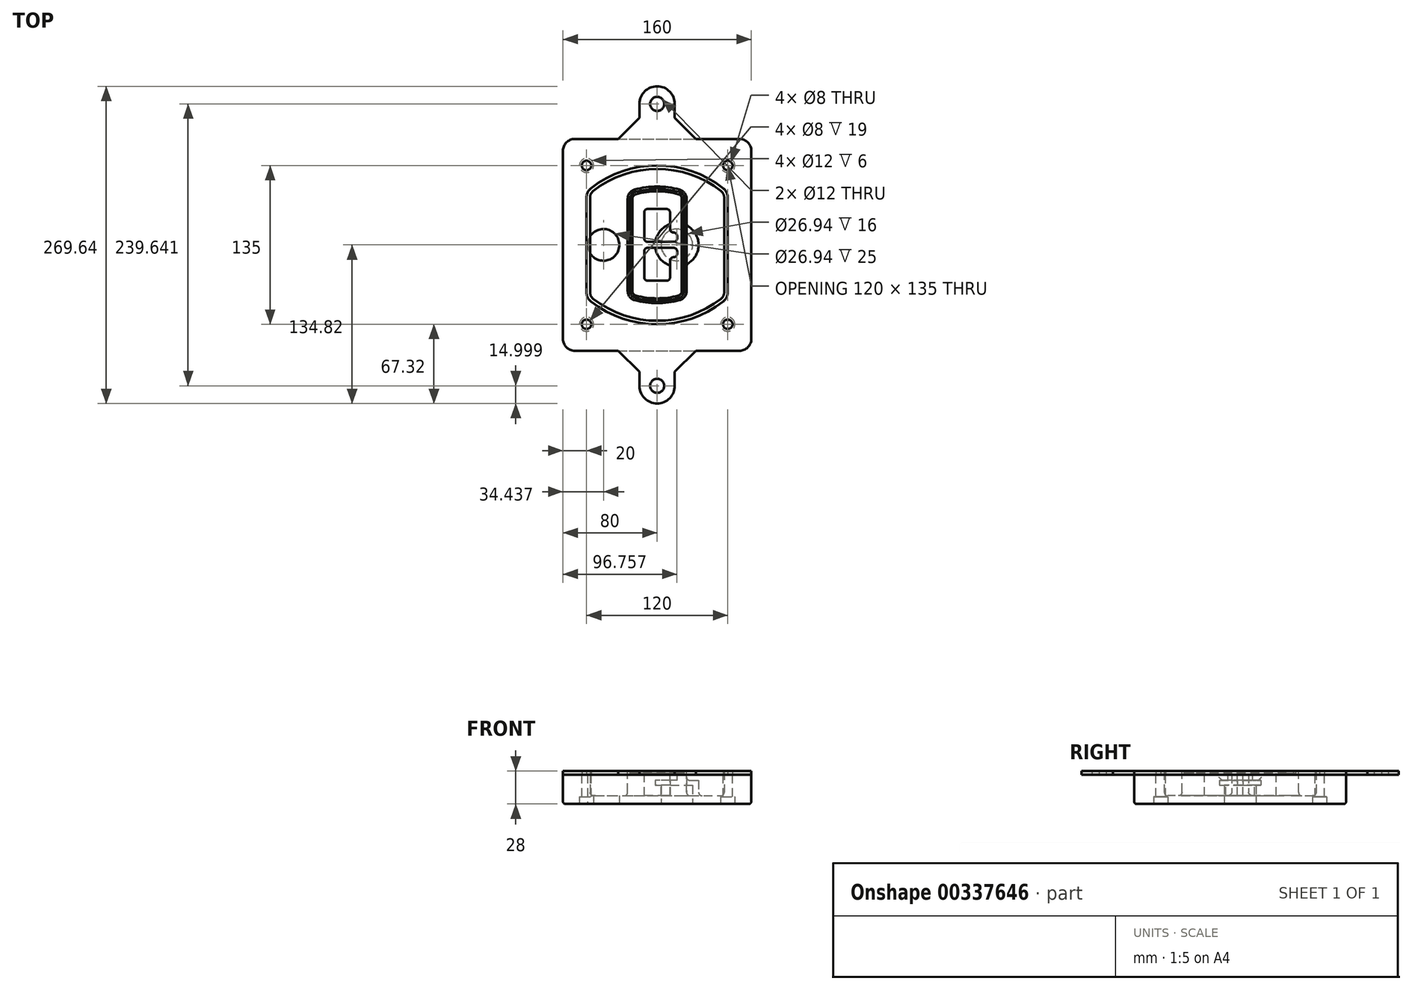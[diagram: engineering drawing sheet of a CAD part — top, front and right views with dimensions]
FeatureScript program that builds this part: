
annotation { "Feature Type Name" : "Feature", "Feature Type Description" : "" }
export const myFeature = defineFeature(function(context is Context, id is Id, definition is map)
    precondition{}
    {
        {
            var Q0;
            Q0=qCreatedBy(makeId("Top.planeOp"),FACE);
            var sketch = newSketch(context, id + "F0", { "sketchPlane" : qUnion([Q0])});
            skPoint(sketch, "E0.rect.middle", {"position": v(0, 0) * mm});
            skLineSegment(sketch, "E1.bottom", {"start": v(-70, -90) * mm, "end": v(70, -90) * mm});
            skLineSegment(sketch, "E1.top", {"start": v(-70, 90) * mm, "end": v(70, 90) * mm});
            skLineSegment(sketch, "E1.left", {"start": v(-80, -80) * mm, "end": v(-80, 80) * mm});
            skLineSegment(sketch, "E1.right", {"start": v(80, -80) * mm, "end": v(80, 80) * mm});
            skLineSegment(sketch, "E2", {"start": v(-80, 90) * mm, "end": v(80, -90) * mm, "construction": true});
            skLineSegment(sketch, "E3", {"start": v(80, 90) * mm, "end": v(-80, -90) * mm, "construction": true});
            skCircle(sketch, "E4", {"center": v(-60, 67.5) * mm, "radius": 4 * mm});
            skCircle(sketch, "E5", {"center": v(60, 67.5) * mm, "radius": 4 * mm});
            skCircle(sketch, "E6", {"center": v(60, -67.5) * mm, "radius": 4 * mm});
            skCircle(sketch, "E7", {"center": v(-60, -67.5) * mm, "radius": 4 * mm});
            skLineSegment(sketch, "E8", {"start": v(-60, 67.5) * mm, "end": v(60, 67.5) * mm, "construction": true});
            skLineSegment(sketch, "E9", {"start": v(60, 67.5) * mm, "end": v(60, -67.5) * mm, "construction": true});
            skLineSegment(sketch, "E10", {"start": v(60, -67.5) * mm, "end": v(-60, -67.5) * mm, "construction": true});
            skLineSegment(sketch, "E11", {"start": v(-60, -67.5) * mm, "end": v(-60, 67.5) * mm, "construction": true});
            skLineSegment(sketch, "E12", {"start": v(-60, 40.3) * mm, "end": v(-60, -40.3) * mm});
            skLineSegment(sketch, "E13", {"start": v(60, 40.3) * mm, "end": v(60, -40.3) * mm});
            skArc(sketch, "E14", {"start": v(56.15, 48.18) * mm, "mid": v(0, 67.5) * mm, "end": v(-56.15, 48.18) * mm});
            skArc(sketch, "E15", {"start": v(-56.15, -48.18) * mm, "mid": v(0, -67.5) * mm, "end": v(56.15, -48.18) * mm});
            skLineSegment(sketch, "E16", {"start": v(-60, 0) * mm, "end": v(60, 0) * mm, "construction": true});
            skPoint(sketch, "E17.visualSharp", {"position": v(-60, -45) * mm});
            skArc(sketch, "E17.filletArc", {"start": v(-60, -40.3) * mm, "mid": v(-58.99, -44.68) * mm, "end": v(-56.15, -48.18) * mm});
            skPoint(sketch, "E18.visualSharp", {"position": v(-60, 45) * mm});
            skArc(sketch, "E18.filletArc", {"start": v(-56.15, 48.18) * mm, "mid": v(-58.99, 44.68) * mm, "end": v(-60, 40.3) * mm});
            skPoint(sketch, "E19.visualSharp", {"position": v(60, 45) * mm});
            skArc(sketch, "E19.filletArc", {"start": v(60, 40.3) * mm, "mid": v(58.99, 44.68) * mm, "end": v(56.15, 48.18) * mm});
            skPoint(sketch, "E20.visualSharp", {"position": v(60, -45) * mm});
            skArc(sketch, "E20.filletArc", {"start": v(56.15, -48.18) * mm, "mid": v(58.99, -44.68) * mm, "end": v(60, -40.3) * mm});
            skPoint(sketch, "E21.visualSharp", {"position": v(-80, 90) * mm});
            skArc(sketch, "E21.filletArc", {"start": v(-70, 90) * mm, "mid": v(-77.07, 87.07) * mm, "end": v(-80, 80) * mm});
            skPoint(sketch, "E22.visualSharp", {"position": v(80, 90) * mm});
            skArc(sketch, "E22.filletArc", {"start": v(80, 80) * mm, "mid": v(77.07, 87.07) * mm, "end": v(70, 90) * mm});
            skPoint(sketch, "E23.visualSharp", {"position": v(80, -90) * mm});
            skArc(sketch, "E23.filletArc", {"start": v(70, -90) * mm, "mid": v(77.07, -87.07) * mm, "end": v(80, -80) * mm});
            skPoint(sketch, "E24.visualSharp", {"position": v(-80, -90) * mm});
            skArc(sketch, "E24.filletArc", {"start": v(-80, -80) * mm, "mid": v(-77.07, -87.07) * mm, "end": v(-70, -90) * mm});
            skArc(sketch, "E25.0", {"start": v(57, 40.3) * mm, "mid": v(56.3, 43.36) * mm, "end": v(54.3, 45.81) * mm});
            skLineSegment(sketch, "E25.1", {"start": v(57, 40.3) * mm, "end": v(57, -40.3) * mm});
            skArc(sketch, "E25.2", {"start": v(54.3, -45.81) * mm, "mid": v(56.3, -43.36) * mm, "end": v(57, -40.3) * mm});
            skArc(sketch, "E25.3", {"start": v(-54.3, -45.81) * mm, "mid": v(0, -64.5) * mm, "end": v(54.3, -45.81) * mm});
            skArc(sketch, "E25.4", {"start": v(-57, -40.3) * mm, "mid": v(-56.3, -43.36) * mm, "end": v(-54.3, -45.81) * mm});
            skArc(sketch, "E25.5", {"start": v(54.3, 45.81) * mm, "mid": v(0, 64.5) * mm, "end": v(-54.3, 45.81) * mm});
            skLineSegment(sketch, "E25.6", {"start": v(-57, 40.3) * mm, "end": v(-57, -40.3) * mm});
            skArc(sketch, "E25.7", {"start": v(-54.3, 45.81) * mm, "mid": v(-56.3, 43.36) * mm, "end": v(-57, 40.3) * mm});
            skArc(sketch, "E26.0", {"start": v(-58.62, 51.33) * mm, "mid": v(-62.58, 46.43) * mm, "end": v(-64, 40.3) * mm});
            skArc(sketch, "E26.1", {"start": v(58.62, 51.33) * mm, "mid": v(0, 71.5) * mm, "end": v(-58.62, 51.33) * mm});
            skArc(sketch, "E26.2", {"start": v(64, 40.3) * mm, "mid": v(62.58, 46.43) * mm, "end": v(58.62, 51.33) * mm});
            skLineSegment(sketch, "E26.3", {"start": v(64, 40.3) * mm, "end": v(64, -40.3) * mm});
            skArc(sketch, "E26.4", {"start": v(58.62, -51.33) * mm, "mid": v(62.58, -46.43) * mm, "end": v(64, -40.3) * mm});
            skLineSegment(sketch, "E26.5", {"start": v(-64, 40.3) * mm, "end": v(-64, -40.3) * mm});
            skArc(sketch, "E26.6", {"start": v(-58.62, -51.33) * mm, "mid": v(0, -71.5) * mm, "end": v(58.62, -51.33) * mm});
            skArc(sketch, "E26.7", {"start": v(-64, -40.3) * mm, "mid": v(-62.58, -46.43) * mm, "end": v(-58.62, -51.33) * mm});
            skSolve(sketch);
        }
        {
            var Q0;
            Q0=makeQuery(id+"F0.imprint","IMPRINT",FACE,{"disambiguationData":[TD([[makeQuery(id+"F0.imprint","IMPRINT",EDGE,{"derivedFrom":sQuery(id+"F0.wireOp",EDGE,"E1.bottom")}),1.0]])]});
            var Q1;
            Q1=makeQuery(id+"F0.imprint","IMPRINT",FACE,{"disambiguationData":[TD([[makeQuery(id+"F0.imprint","IMPRINT",EDGE,{"derivedFrom":sQuery(id+"F0.wireOp",EDGE,"E12")}),1.0]])]});
            var Q2;
            Q2=makeQuery(id+"F0.imprint","IMPRINT",FACE,{"disambiguationData":[TD([[makeQuery(id+"F0.imprint","IMPRINT",EDGE,{"derivedFrom":sQuery(id+"F0.wireOp",EDGE,"E25.0")}),1.0]])]});
            var Q3;
            Q3=makeQuery(id+"F0.imprint","IMPRINT",FACE,{"disambiguationData":[TD([[makeQuery(id+"F0.imprint","IMPRINT",EDGE,{"derivedFrom":sQuery(id+"F0.wireOp",EDGE,"E12")}),-1.0]])]});
            extrude(context, id + "F1", {"entities" : qUnion([Q0, Q1, Q2, Q3]), "oppositeDirection" : true, "depth" : 25 * mm});
        }
        {
            var Q0;
            Q0=makeQuery(id+"F0.imprint","IMPRINT",FACE,{"disambiguationData":[TD([[makeQuery(id+"F0.imprint","IMPRINT",EDGE,{"derivedFrom":sQuery(id+"F0.wireOp",EDGE,"E12")}),1.0]])]});
            extrude(context, id + "F2", {"entities" : qUnion([Q0]), "operationType" : NewBodyOperationType.ADD, "depth" : 3 * mm});
        }
        {
            var Q0;
            Q0=makeQuery(id+"F0.imprint","IMPRINT",FACE,{"disambiguationData":[TD([[makeQuery(id+"F0.imprint","IMPRINT",EDGE,{"derivedFrom":sQuery(id+"F0.wireOp",EDGE,"E25.0")}),1.0]])]});
            extrude(context, id + "F3", {"entities" : qUnion([Q0]), "operationType" : NewBodyOperationType.REMOVE, "oppositeDirection" : true, "depth" : 18 * mm});
        }
        {
            var Q0;
            Q0=makeQuery(id+"F2.opExtrude","CAP_FACE",FACE,{"disambiguationData":[OSD([sQuery(id+"F0.wireOp",EDGE,"E12"),sQuery(id+"F0.wireOp",EDGE,"E13"),sQuery(id+"F0.wireOp",EDGE,"E14"),sQuery(id+"F0.wireOp",EDGE,"E15"),sQuery(id+"F0.wireOp",EDGE,"E17.filletArc"),sQuery(id+"F0.wireOp",EDGE,"E18.filletArc"),sQuery(id+"F0.wireOp",EDGE,"E19.filletArc"),sQuery(id+"F0.wireOp",EDGE,"E20.filletArc"),sQuery(id+"F0.wireOp",EDGE,"E25.0"),sQuery(id+"F0.wireOp",EDGE,"E25.1"),sQuery(id+"F0.wireOp",EDGE,"E25.2"),sQuery(id+"F0.wireOp",EDGE,"E25.3"),sQuery(id+"F0.wireOp",EDGE,"E25.4"),sQuery(id+"F0.wireOp",EDGE,"E25.5"),sQuery(id+"F0.wireOp",EDGE,"E25.6"),sQuery(id+"F0.wireOp",EDGE,"E25.7")])],"isStart":false});
            var sketch = newSketch(context, id + "F4", { "sketchPlane" : qUnion([Q0])});
            skArc(sketch, "E27.0", {"start": v(-19.08, -46.97) * mm, "mid": v(0, -49.5) * mm, "end": v(19.08, -46.97) * mm});
            skArc(sketch, "E28.0", {"start": v(19.08, 46.97) * mm, "mid": v(0, 49.5) * mm, "end": v(-19.08, 46.97) * mm});
            skLineSegment(sketch, "E29", {"start": v(-25, 39.25) * mm, "end": v(-25, -39.25) * mm});
            skLineSegment(sketch, "E30", {"start": v(25, 39.25) * mm, "end": v(25, -39.25) * mm});
            skLineSegment(sketch, "E31", {"start": v(-25, 45.1) * mm, "end": v(25, 45.1) * mm, "construction": true});
            skLineSegment(sketch, "E32", {"start": v(-25, -45.1) * mm, "end": v(25, -45.1) * mm, "construction": true});
            skPoint(sketch, "E33.visualSharp", {"position": v(-25, 45.1) * mm});
            skArc(sketch, "E33.filletArc", {"start": v(-19.08, 46.97) * mm, "mid": v(-23.35, 44.11) * mm, "end": v(-25, 39.25) * mm});
            skPoint(sketch, "E34.visualSharp", {"position": v(25, 45.1) * mm});
            skArc(sketch, "E34.filletArc", {"start": v(25, 39.25) * mm, "mid": v(23.35, 44.11) * mm, "end": v(19.08, 46.97) * mm});
            skPoint(sketch, "E35.visualSharp", {"position": v(25, -45.1) * mm});
            skArc(sketch, "E35.filletArc", {"start": v(19.08, -46.97) * mm, "mid": v(23.35, -44.11) * mm, "end": v(25, -39.25) * mm});
            skPoint(sketch, "E36.visualSharp", {"position": v(-25, -45.1) * mm});
            skArc(sketch, "E36.filletArc", {"start": v(-25, -39.25) * mm, "mid": v(-23.35, -44.11) * mm, "end": v(-19.08, -46.97) * mm});
            skArc(sketch, "E37.0", {"start": v(54.3, 45.81) * mm, "mid": v(0, 64.5) * mm, "end": v(-54.3, 45.81) * mm});
            skArc(sketch, "E37.1", {"start": v(-54.3, 45.81) * mm, "mid": v(-56.3, 43.36) * mm, "end": v(-57, 40.3) * mm});
            skLineSegment(sketch, "E37.2", {"start": v(-57, 40.3) * mm, "end": v(-57, -40.3) * mm});
            skArc(sketch, "E37.3", {"start": v(-57, -40.3) * mm, "mid": v(-56.3, -43.36) * mm, "end": v(-54.3, -45.81) * mm});
            skArc(sketch, "E37.4", {"start": v(-54.3, -45.81) * mm, "mid": v(0, -64.5) * mm, "end": v(54.3, -45.81) * mm});
            skArc(sketch, "E37.5", {"start": v(54.3, -45.81) * mm, "mid": v(56.3, -43.36) * mm, "end": v(57, -40.3) * mm});
            skLineSegment(sketch, "E37.6", {"start": v(57, 40.3) * mm, "end": v(57, -40.3) * mm});
            skArc(sketch, "E37.7", {"start": v(57, 40.3) * mm, "mid": v(56.3, 43.36) * mm, "end": v(54.3, 45.81) * mm});
            skLineSegment(sketch, "E38.0", {"start": v(23, 39.25) * mm, "end": v(23, -39.25) * mm});
            skArc(sketch, "E38.1", {"start": v(18.56, -45.04) * mm, "mid": v(21.76, -42.9) * mm, "end": v(23, -39.25) * mm});
            skArc(sketch, "E38.2", {"start": v(-18.56, -45.04) * mm, "mid": v(0, -47.5) * mm, "end": v(18.56, -45.04) * mm});
            skArc(sketch, "E38.3", {"start": v(-23, -39.25) * mm, "mid": v(-21.76, -42.9) * mm, "end": v(-18.56, -45.04) * mm});
            skLineSegment(sketch, "E38.4", {"start": v(-23, 39.25) * mm, "end": v(-23, -39.25) * mm});
            skArc(sketch, "E38.5", {"start": v(23, 39.25) * mm, "mid": v(21.76, 42.9) * mm, "end": v(18.56, 45.04) * mm});
            skArc(sketch, "E38.6", {"start": v(-18.56, 45.04) * mm, "mid": v(-21.76, 42.9) * mm, "end": v(-23, 39.25) * mm});
            skArc(sketch, "E38.7", {"start": v(18.56, 45.04) * mm, "mid": v(0, 47.5) * mm, "end": v(-18.56, 45.04) * mm});
            skArc(sketch, "E39.0", {"start": v(21, 39.25) * mm, "mid": v(20.18, 41.68) * mm, "end": v(18.04, 43.1) * mm});
            skLineSegment(sketch, "E39.1", {"start": v(21, 39.25) * mm, "end": v(21, -39.25) * mm});
            skArc(sketch, "E39.2", {"start": v(18.04, -43.1) * mm, "mid": v(20.18, -41.68) * mm, "end": v(21, -39.25) * mm});
            skArc(sketch, "E39.3", {"start": v(-18.04, -43.1) * mm, "mid": v(0, -45.5) * mm, "end": v(18.04, -43.1) * mm});
            skArc(sketch, "E39.4", {"start": v(-21, -39.25) * mm, "mid": v(-20.18, -41.68) * mm, "end": v(-18.04, -43.1) * mm});
            skArc(sketch, "E39.5", {"start": v(18.04, 43.1) * mm, "mid": v(0, 45.5) * mm, "end": v(-18.04, 43.1) * mm});
            skLineSegment(sketch, "E39.6", {"start": v(-21, 39.25) * mm, "end": v(-21, -39.25) * mm});
            skArc(sketch, "E39.7", {"start": v(-18.04, 43.1) * mm, "mid": v(-20.18, 41.68) * mm, "end": v(-21, 39.25) * mm});
            skLineSegment(sketch, "E40", {"start": v(-25, 0) * mm, "end": v(25, 0) * mm, "construction": true});
            skLineSegment(sketch, "E41", {"start": v(-11, 5.5) * mm, "end": v(-11, 27.5) * mm});
            skLineSegment(sketch, "E42", {"start": v(-8, 30.5) * mm, "end": v(8, 30.5) * mm});
            skLineSegment(sketch, "E43", {"start": v(11, 27.5) * mm, "end": v(11, 13.5) * mm});
            skLineSegment(sketch, "E44", {"start": v(14, 10.5) * mm, "end": v(14, 10.5) * mm});
            skLineSegment(sketch, "E45", {"start": v(17, 7.5) * mm, "end": v(17, 5.5) * mm});
            skLineSegment(sketch, "E46", {"start": v(14, 2.5) * mm, "end": v(-8, 2.5) * mm});
            skPoint(sketch, "E47.visualSharp", {"position": v(-11, 30.5) * mm});
            skArc(sketch, "E47.filletArc", {"start": v(-8, 30.5) * mm, "mid": v(-10.12, 29.62) * mm, "end": v(-11, 27.5) * mm});
            skPoint(sketch, "E48.visualSharp", {"position": v(11, 30.5) * mm});
            skArc(sketch, "E48.filletArc", {"start": v(11, 27.5) * mm, "mid": v(10.12, 29.62) * mm, "end": v(8, 30.5) * mm});
            skPoint(sketch, "E49.visualSharp", {"position": v(11, 10.5) * mm});
            skArc(sketch, "E49.filletArc", {"start": v(11, 13.5) * mm, "mid": v(11.88, 11.38) * mm, "end": v(14, 10.5) * mm});
            skPoint(sketch, "E50.visualSharp", {"position": v(17, 10.5) * mm});
            skArc(sketch, "E50.filletArc", {"start": v(17, 7.5) * mm, "mid": v(16.12, 9.62) * mm, "end": v(14, 10.5) * mm});
            skPoint(sketch, "E51.visualSharp", {"position": v(17, 2.5) * mm});
            skArc(sketch, "E51.filletArc", {"start": v(14, 2.5) * mm, "mid": v(16.12, 3.38) * mm, "end": v(17, 5.5) * mm});
            skPoint(sketch, "E52.visualSharp", {"position": v(-11, 2.5) * mm});
            skArc(sketch, "E52.filletArc", {"start": v(-11, 5.5) * mm, "mid": v(-10.12, 3.38) * mm, "end": v(-8, 2.5) * mm});
            skLineSegment(sketch, "E53.0.MirrorCS", {"start": v(14, -2.5) * mm, "end": v(-8, -2.5) * mm});
            skArc(sketch, "E54.0.MirrorCS", {"start": v(-11, -5.5) * mm, "mid": v(-10.12, -3.38) * mm, "end": v(-8, -2.5) * mm});
            skLineSegment(sketch, "E55.0.MirrorCS", {"start": v(-11, -5.5) * mm, "end": v(-11, -27.5) * mm});
            skArc(sketch, "E56.0.MirrorCS", {"start": v(-8, -30.5) * mm, "mid": v(-10.12, -29.62) * mm, "end": v(-11, -27.5) * mm});
            skLineSegment(sketch, "E57.0.MirrorCS", {"start": v(-8, -30.5) * mm, "end": v(8, -30.5) * mm});
            skArc(sketch, "E58.0.MirrorCS", {"start": v(11, -27.5) * mm, "mid": v(10.12, -29.62) * mm, "end": v(8, -30.5) * mm});
            skLineSegment(sketch, "E59.0.MirrorCS", {"start": v(11, -27.5) * mm, "end": v(11, -13.5) * mm});
            skArc(sketch, "E60.0.MirrorCS", {"start": v(11, -13.5) * mm, "mid": v(11.88, -11.38) * mm, "end": v(14, -10.5) * mm});
            skArc(sketch, "E61.0.MirrorCS", {"start": v(17, -7.5) * mm, "mid": v(16.12, -9.62) * mm, "end": v(14, -10.5) * mm});
            skLineSegment(sketch, "E62.0.MirrorCS", {"start": v(17, -7.5) * mm, "end": v(17, -5.5) * mm});
            skArc(sketch, "E63.0.MirrorCS", {"start": v(14, -2.5) * mm, "mid": v(16.12, -3.38) * mm, "end": v(17, -5.5) * mm});
            skSolve(sketch);
        }
        {
            var Q0;
            Q0=makeQuery(id+"F4.imprint","IMPRINT",FACE,{"disambiguationData":[TD([[makeQuery(id+"F4.imprint","IMPRINT",EDGE,{"derivedFrom":sQuery(id+"F4.wireOp",EDGE,"E27.0")}),1.0]])]});
            var Q1;
            Q1=makeQuery(id+"F4.imprint","IMPRINT",FACE,{"disambiguationData":[TD([[makeQuery(id+"F4.imprint","IMPRINT",EDGE,{"derivedFrom":sQuery(id+"F4.wireOp",EDGE,"E38.0")}),-1.0]])]});
            var Q2;
            Q2=makeQuery(id+"F4.imprint","IMPRINT",FACE,{"disambiguationData":[TD([[makeQuery(id+"F4.imprint","IMPRINT",EDGE,{"derivedFrom":sQuery(id+"F4.wireOp",EDGE,"E39.0")}),1.0]])]});
            extrude(context, id + "F5", {"entities" : qUnion([Q0, Q1, Q2]), "operationType" : NewBodyOperationType.ADD, "endBound" : BoundingType.UP_TO_NEXT, "oppositeDirection" : true, "depth" : 25 * mm});
        }
        {
            var Q0;
            Q0=makeQuery(id+"F4.imprint","IMPRINT",FACE,{"disambiguationData":[TD([[makeQuery(id+"F4.imprint","IMPRINT",EDGE,{"derivedFrom":sQuery(id+"F4.wireOp",EDGE,"E38.0")}),-1.0]])]});
            extrude(context, id + "F6", {"entities" : qUnion([Q0]), "operationType" : NewBodyOperationType.REMOVE, "oppositeDirection" : true, "depth" : 2 * mm});
        }
        {
            var Q0;
            Q0=makeQuery(id+"F1.opExtrude","CAP_FACE",FACE,{"disambiguationData":[OSD([sQuery(id+"F0.wireOp",EDGE,"E1.bottom"),sQuery(id+"F0.wireOp",EDGE,"E1.top"),sQuery(id+"F0.wireOp",EDGE,"E1.left"),sQuery(id+"F0.wireOp",EDGE,"E1.right"),sQuery(id+"F0.wireOp",EDGE,"E4"),sQuery(id+"F0.wireOp",EDGE,"E5"),sQuery(id+"F0.wireOp",EDGE,"E6"),sQuery(id+"F0.wireOp",EDGE,"E7"),sQuery(id+"F0.wireOp",EDGE,"E21.filletArc"),sQuery(id+"F0.wireOp",EDGE,"E22.filletArc"),sQuery(id+"F0.wireOp",EDGE,"E23.filletArc"),sQuery(id+"F0.wireOp",EDGE,"E24.filletArc")])],"isStart":false});
            var sketch = newSketch(context, id + "F7", { "sketchPlane" : qUnion([Q0])});
            skCircle(sketch, "E64", {"center": v(16.76, 0) * mm, "radius": 13.47 * mm});
            skCircle(sketch, "E65", {"center": v(-45.56, 0) * mm, "radius": 13.47 * mm});
            skLineSegment(sketch, "E66", {"start": v(80, 0) * mm, "end": v(-80, 0) * mm});
            skCircle(sketch, "E67", {"center": v(16.76, 0) * mm, "radius": 18.47 * mm});
            skCircle(sketch, "E68", {"center": v(60, -67.5) * mm, "radius": 6 * mm});
            skCircle(sketch, "E69", {"center": v(-60, -67.5) * mm, "radius": 6 * mm});
            skCircle(sketch, "E70", {"center": v(-60, 67.5) * mm, "radius": 6 * mm});
            skCircle(sketch, "E71", {"center": v(60, 67.5) * mm, "radius": 6 * mm});
            skSolve(sketch);
        }
        {
            var Q0;
            {var subQ1=sQuery(id+"F7.wireOp",EDGE,"E66");var subQ4=sQuery(id+"F7.wireOp",EDGE,"E64");var subQ6=makeQuery(id+"F7.imprint","INTERSECT",VERTEX,{"disambiguationData":[OD(0.0)],"derivedFrom":[subQ4,subQ1]});Q0=makeQuery(id+"F7.imprint","IMPRINT",FACE,{"disambiguationData":[TD([[makeQuery(id+"F7.imprint","IMPRINT",EDGE,{"disambiguationData":[TD([[subQ6,-1.0]])],"derivedFrom":subQ4}),-1.0]])]});}
            var Q1;
            {var subQ0=sQuery(id+"F7.wireOp",EDGE,"E66");var subQ1=sQuery(id+"F7.wireOp",EDGE,"E64");var subQ3=makeQuery(id+"F7.imprint","INTERSECT",VERTEX,{"disambiguationData":[OD(0.0)],"derivedFrom":[subQ1,subQ0]});Q1=makeQuery(id+"F7.imprint","IMPRINT",FACE,{"disambiguationData":[TD([[makeQuery(id+"F7.imprint","IMPRINT",EDGE,{"disambiguationData":[TD([[subQ3,-1.0]])],"derivedFrom":subQ1}),1.0]])]});}
            var Q2;
            {var subQ0=sQuery(id+"F7.wireOp",EDGE,"E66");var subQ1=sQuery(id+"F7.wireOp",EDGE,"E64");var subQ3=makeQuery(id+"F7.imprint","INTERSECT",VERTEX,{"disambiguationData":[OD(0.0)],"derivedFrom":[subQ1,subQ0]});Q2=makeQuery(id+"F7.imprint","IMPRINT",FACE,{"disambiguationData":[TD([[makeQuery(id+"F7.imprint","IMPRINT",EDGE,{"disambiguationData":[TD([[subQ3,1.0]])],"derivedFrom":subQ1}),1.0]])]});}
            var Q3;
            {var subQ1=sQuery(id+"F7.wireOp",EDGE,"E66");var subQ4=sQuery(id+"F7.wireOp",EDGE,"E64");var subQ6=makeQuery(id+"F7.imprint","INTERSECT",VERTEX,{"disambiguationData":[OD(0.0)],"derivedFrom":[subQ4,subQ1]});Q3=makeQuery(id+"F7.imprint","IMPRINT",FACE,{"disambiguationData":[TD([[makeQuery(id+"F7.imprint","IMPRINT",EDGE,{"disambiguationData":[TD([[subQ6,1.0]])],"derivedFrom":subQ4}),-1.0]])]});}
            extrude(context, id + "F8", {"entities" : qUnion([Q0, Q1, Q2, Q3]), "operationType" : NewBodyOperationType.ADD, "oppositeDirection" : true, "depth" : 20 * mm});
        }
        {
            var Q0;
            {var subQ0=sQuery(id+"F7.wireOp",EDGE,"E66");var subQ1=sQuery(id+"F7.wireOp",EDGE,"E64");var subQ3=makeQuery(id+"F7.imprint","INTERSECT",VERTEX,{"disambiguationData":[OD(0.0)],"derivedFrom":[subQ1,subQ0]});Q0=makeQuery(id+"F7.imprint","IMPRINT",FACE,{"disambiguationData":[TD([[makeQuery(id+"F7.imprint","IMPRINT",EDGE,{"disambiguationData":[TD([[subQ3,-1.0]])],"derivedFrom":subQ1}),1.0]])]});}
            var Q1;
            {var subQ0=sQuery(id+"F7.wireOp",EDGE,"E66");var subQ1=sQuery(id+"F7.wireOp",EDGE,"E64");var subQ3=makeQuery(id+"F7.imprint","INTERSECT",VERTEX,{"disambiguationData":[OD(0.0)],"derivedFrom":[subQ1,subQ0]});Q1=makeQuery(id+"F7.imprint","IMPRINT",FACE,{"disambiguationData":[TD([[makeQuery(id+"F7.imprint","IMPRINT",EDGE,{"disambiguationData":[TD([[subQ3,1.0]])],"derivedFrom":subQ1}),1.0]])]});}
            extrude(context, id + "F9", {"entities" : qUnion([Q0, Q1]), "operationType" : NewBodyOperationType.REMOVE, "oppositeDirection" : true, "depth" : 16 * mm});
        }
        {
            var Q0;
            {var subQ0=sQuery(id+"F7.wireOp",EDGE,"E66");var subQ1=sQuery(id+"F7.wireOp",EDGE,"E65");var subQ3=makeQuery(id+"F7.imprint","INTERSECT",VERTEX,{"disambiguationData":[OD(0.0)],"derivedFrom":[subQ1,subQ0]});Q0=makeQuery(id+"F7.imprint","IMPRINT",FACE,{"disambiguationData":[TD([[makeQuery(id+"F7.imprint","IMPRINT",EDGE,{"disambiguationData":[TD([[subQ3,-1.0]])],"derivedFrom":subQ1}),1.0]])]});}
            var Q1;
            {var subQ0=sQuery(id+"F7.wireOp",EDGE,"E66");var subQ1=sQuery(id+"F7.wireOp",EDGE,"E65");var subQ3=makeQuery(id+"F7.imprint","INTERSECT",VERTEX,{"disambiguationData":[OD(0.0)],"derivedFrom":[subQ1,subQ0]});Q1=makeQuery(id+"F7.imprint","IMPRINT",FACE,{"disambiguationData":[TD([[makeQuery(id+"F7.imprint","IMPRINT",EDGE,{"disambiguationData":[TD([[subQ3,1.0]])],"derivedFrom":subQ1}),1.0]])]});}
            extrude(context, id + "F10", {"entities" : qUnion([Q0, Q1]), "operationType" : NewBodyOperationType.REMOVE, "oppositeDirection" : true, "depth" : 25 * mm});
        }
        {
            var Q0;
            Q0=makeQuery(id+"F7.imprint","IMPRINT",FACE,{"disambiguationData":[TD([[makeQuery(id+"F7.imprint","IMPRINT",EDGE,{"derivedFrom":sQuery(id+"F7.wireOp",EDGE,"E68")}),1.0]])]});
            var Q1;
            Q1=makeQuery(id+"F7.imprint","IMPRINT",FACE,{"disambiguationData":[TD([[makeQuery(id+"F7.imprint","IMPRINT",EDGE,{"derivedFrom":makeQuery(id+"F1.opExtrude","CAP_EDGE",EDGE,{"disambiguationData":[OSD([sQuery(id+"F0.wireOp",EDGE,"E5")])],"isStart":false})}),-1.0]])]});
            var Q2;
            Q2=makeQuery(id+"F7.imprint","IMPRINT",FACE,{"disambiguationData":[TD([[makeQuery(id+"F7.imprint","IMPRINT",EDGE,{"derivedFrom":sQuery(id+"F7.wireOp",EDGE,"E69")}),1.0]])]});
            var Q3;
            Q3=makeQuery(id+"F7.imprint","IMPRINT",FACE,{"disambiguationData":[TD([[makeQuery(id+"F7.imprint","IMPRINT",EDGE,{"derivedFrom":makeQuery(id+"F1.opExtrude","CAP_EDGE",EDGE,{"disambiguationData":[OSD([sQuery(id+"F0.wireOp",EDGE,"E4")])],"isStart":false})}),-1.0]])]});
            var Q4;
            Q4=makeQuery(id+"F7.imprint","IMPRINT",FACE,{"disambiguationData":[TD([[makeQuery(id+"F7.imprint","IMPRINT",EDGE,{"derivedFrom":sQuery(id+"F7.wireOp",EDGE,"E70")}),1.0]])]});
            var Q5;
            Q5=makeQuery(id+"F7.imprint","IMPRINT",FACE,{"disambiguationData":[TD([[makeQuery(id+"F7.imprint","IMPRINT",EDGE,{"derivedFrom":makeQuery(id+"F1.opExtrude","CAP_EDGE",EDGE,{"disambiguationData":[OSD([sQuery(id+"F0.wireOp",EDGE,"E7")])],"isStart":false})}),-1.0]])]});
            var Q6;
            Q6=makeQuery(id+"F7.imprint","IMPRINT",FACE,{"disambiguationData":[TD([[makeQuery(id+"F7.imprint","IMPRINT",EDGE,{"derivedFrom":sQuery(id+"F7.wireOp",EDGE,"E71")}),1.0]])]});
            var Q7;
            Q7=makeQuery(id+"F7.imprint","IMPRINT",FACE,{"disambiguationData":[TD([[makeQuery(id+"F7.imprint","IMPRINT",EDGE,{"derivedFrom":makeQuery(id+"F1.opExtrude","CAP_EDGE",EDGE,{"disambiguationData":[OSD([sQuery(id+"F0.wireOp",EDGE,"E6")])],"isStart":false})}),-1.0]])]});
            extrude(context, id + "F11", {"entities" : qUnion([Q0, Q1, Q2, Q3, Q4, Q5, Q6, Q7]), "operationType" : NewBodyOperationType.REMOVE, "oppositeDirection" : true, "depth" : 6 * mm});
        }
        {
            var Q0;
            Q0=makeQuery(id+"F9.boolean.opBoolean","COPY",FACE,{"derivedFrom":makeQuery(id+"F9.opExtrude","CAP_FACE",FACE,{"disambiguationData":[OSD([sQuery(id+"F7.wireOp",EDGE,"E64")])],"isStart":false})});
            var sketch = newSketch(context, id + "F12", { "sketchPlane" : qUnion([Q0])});
            skArc(sketch, "E72.0", {"start": v(11, 17.55) * mm, "mid": v(2.57, 11.82) * mm, "end": v(-1.54, 2.5) * mm});
            skArc(sketch, "E72.1", {"start": v(-1.54, -2.5) * mm, "mid": v(2.57, -11.82) * mm, "end": v(11, -17.55) * mm});
            skLineSegment(sketch, "E73", {"start": v(-1.54, -2.5) * mm, "end": v(14, -2.5) * mm});
            skLineSegment(sketch, "E74.0", {"start": v(14, 2.5) * mm, "end": v(-1.54, 2.5) * mm});
            skArc(sketch, "E74.1", {"start": v(14, 2.5) * mm, "mid": v(16.12, 3.38) * mm, "end": v(17, 5.5) * mm});
            skLineSegment(sketch, "E74.2", {"start": v(17, 7.5) * mm, "end": v(17, 5.5) * mm});
            skArc(sketch, "E74.3", {"start": v(17, 7.5) * mm, "mid": v(16.12, 9.62) * mm, "end": v(14, 10.5) * mm});
            skArc(sketch, "E74.4", {"start": v(11, 13.5) * mm, "mid": v(11.88, 11.38) * mm, "end": v(14, 10.5) * mm});
            skLineSegment(sketch, "E74.5", {"start": v(11, 17.55) * mm, "end": v(11, 13.5) * mm});
            skLineSegment(sketch, "E74.7", {"start": v(14, -2.5) * mm, "end": v(-1.54, -2.5) * mm});
            skArc(sketch, "E74.8", {"start": v(14, -2.5) * mm, "mid": v(16.12, -3.38) * mm, "end": v(17, -5.5) * mm});
            skLineSegment(sketch, "E74.9", {"start": v(17, -7.5) * mm, "end": v(17, -5.5) * mm});
            skArc(sketch, "E74.10", {"start": v(17, -7.5) * mm, "mid": v(16.12, -9.62) * mm, "end": v(14, -10.5) * mm});
            skArc(sketch, "E74.11", {"start": v(11, -13.5) * mm, "mid": v(11.88, -11.38) * mm, "end": v(14, -10.5) * mm});
            skLineSegment(sketch, "E74.12", {"start": v(11, -17.55) * mm, "end": v(11, -13.5) * mm});
            skPoint(sketch, "E75.orphan", {"position": v(11, -27.5) * mm});
            skPoint(sketch, "E76.orphan", {"position": v(-8, -2.5) * mm});
            skPoint(sketch, "E77.orphan", {"position": v(-8, 2.5) * mm});
            skPoint(sketch, "E78.orphan", {"position": v(11, 27.5) * mm});
            skSolve(sketch);
        }
        {
            var Q0;
            {var subQ7=sQuery(id+"F12.wireOp",EDGE,"E72.0");var subQ14=sQuery(id+"F12.wireOp",EDGE,"E72.1");var subQ16=sQuery(id+"F12.wireOp",EDGE,"E74.1");var subQ18=sQuery(id+"F12.wireOp",EDGE,"E74.8");Q0=qUnion([makeQuery(id+"F12.imprint","IMPRINT",FACE,{"disambiguationData":[TD([[makeQuery(id+"F12.imprint","IMPRINT",EDGE,{"derivedFrom":subQ7}),1.0]])]}),makeQuery(id+"F12.imprint","IMPRINT",FACE,{"disambiguationData":[TD([[makeQuery(id+"F12.imprint","IMPRINT",EDGE,{"derivedFrom":subQ14}),1.0]])]}),makeQuery(id+"F12.imprint","IMPRINT",FACE,{"disambiguationData":[TD([[makeQuery(id+"F12.imprint","IMPRINT",EDGE,{"derivedFrom":subQ16}),1.0]])]}),makeQuery(id+"F12.imprint","IMPRINT",FACE,{"disambiguationData":[TD([[makeQuery(id+"F12.imprint","IMPRINT",EDGE,{"derivedFrom":subQ18}),-1.0]])]})]);}
            var Q1;
            Q1=makeQuery(id+"F5.boolean.opBoolean","SPLIT",FACE,{"disambiguationData":[TD([makeQuery(id+"F5.opExtrude","SWEPT_FACE",FACE,{"disambiguationData":[OSD([sQuery(id+"F4.wireOp",EDGE,"E41")])]})])],"derivedFrom":makeQuery(id+"F3.boolean.opBoolean","COPY",FACE,{"derivedFrom":makeQuery(id+"F3.opExtrude","CAP_FACE",FACE,{"disambiguationData":[OSD([sQuery(id+"F0.wireOp",EDGE,"E25.0"),sQuery(id+"F0.wireOp",EDGE,"E25.1"),sQuery(id+"F0.wireOp",EDGE,"E25.2"),sQuery(id+"F0.wireOp",EDGE,"E25.3"),sQuery(id+"F0.wireOp",EDGE,"E25.4"),sQuery(id+"F0.wireOp",EDGE,"E25.5"),sQuery(id+"F0.wireOp",EDGE,"E25.6"),sQuery(id+"F0.wireOp",EDGE,"E25.7")])],"isStart":false})})});
            extrude(context, id + "F13", {"entities" : qUnion([Q0]), "operationType" : NewBodyOperationType.REMOVE, "endBound" : BoundingType.UP_TO_SURFACE, "endBoundEntityFace" : qUnion([Q1]), "depth" : 25 * mm});
        }
        {
            var Q0;
            Q0=makeQuery(id+"F3.boolean.opBoolean","COPY",EDGE,{"derivedFrom":makeQuery(id+"F3.opExtrude","CAP_EDGE",EDGE,{"disambiguationData":[OSD([sQuery(id+"F0.wireOp",EDGE,"E25.6")])],"isStart":false})});
            var Q1;
            Q1=makeQuery(id+"F8.boolean.opBoolean","INTERSECT",EDGE,{"derivedFrom":[makeQuery(id+"F5.opExtrude","SWEPT_FACE",FACE,{"disambiguationData":[OSD([sQuery(id+"F4.wireOp",EDGE,"E30")])]}),makeQuery(id+"F8.opExtrude","CAP_FACE",FACE,{"disambiguationData":[OSD([sQuery(id+"F7.wireOp",EDGE,"E67")])],"isStart":false})]});
            var Q2;
            Q2=makeQuery(id+"F8.boolean.opBoolean","INTERSECT",EDGE,{"disambiguationData":[OD(1.0)],"derivedFrom":[makeQuery(id+"F5.opExtrude","SWEPT_FACE",FACE,{"disambiguationData":[OSD([sQuery(id+"F4.wireOp",EDGE,"E30")])]}),makeQuery(id+"F8.opExtrude","SWEPT_FACE",FACE,{"disambiguationData":[OSD([sQuery(id+"F7.wireOp",EDGE,"E67")])]})]});
            var Q3;
            {var subQ0=sQuery(id+"F4.wireOp",EDGE,"E30");Q3=makeQuery(id+"F8.boolean.opBoolean","SPLIT",EDGE,{"disambiguationData":[TD([makeQuery(id+"F5.opExtrude","SWEPT_FACE",FACE,{"disambiguationData":[OSD([sQuery(id+"F4.wireOp",EDGE,"E35.filletArc")])]})])],"derivedFrom":makeQuery(id+"F5.opExtrude","CAP_EDGE",EDGE,{"disambiguationData":[OSD([subQ0])],"isStart":false})});}
            var Q4;
            {var subQ0=sQuery(id+"F0.wireOp",EDGE,"E25.7");var subQ1=sQuery(id+"F0.wireOp",EDGE,"E25.1");var subQ2=sQuery(id+"F0.wireOp",EDGE,"E25.6");var subQ3=sQuery(id+"F0.wireOp",EDGE,"E25.5");var subQ4=sQuery(id+"F0.wireOp",EDGE,"E25.4");var subQ5=sQuery(id+"F0.wireOp",EDGE,"E25.0");var subQ6=sQuery(id+"F0.wireOp",EDGE,"E25.2");var subQ7=sQuery(id+"F0.wireOp",EDGE,"E25.3");Q4=makeQuery(id+"F8.boolean.opBoolean","INTERSECT",EDGE,{"derivedFrom":[makeQuery(id+"F5.boolean.opBoolean","SPLIT",FACE,{"disambiguationData":[TD([makeQuery(id+"F2.opExtrude","SWEPT_FACE",FACE,{"disambiguationData":[OSD([subQ5])]})])],"derivedFrom":makeQuery(id+"F3.boolean.opBoolean","COPY",FACE,{"derivedFrom":makeQuery(id+"F3.opExtrude","CAP_FACE",FACE,{"disambiguationData":[OSD([subQ5,subQ1,subQ6,subQ7,subQ4,subQ3,subQ2,subQ0])],"isStart":false})})}),makeQuery(id+"F8.opExtrude","SWEPT_FACE",FACE,{"disambiguationData":[OSD([sQuery(id+"F7.wireOp",EDGE,"E67")])]})]});}
            var Q5;
            Q5=makeQuery(id+"F8.boolean.opBoolean","INTERSECT",EDGE,{"disambiguationData":[OD(0.0)],"derivedFrom":[makeQuery(id+"F5.opExtrude","SWEPT_FACE",FACE,{"disambiguationData":[OSD([sQuery(id+"F4.wireOp",EDGE,"E30")])]}),makeQuery(id+"F8.opExtrude","SWEPT_FACE",FACE,{"disambiguationData":[OSD([sQuery(id+"F7.wireOp",EDGE,"E67")])]})]});
            fillet(context, id + "F14", {"entities" : qUnion([Q0, Q1, Q2, Q3, Q4, Q5]), "radius" : 3 * mm, "tangentPropagation" : true, "allowEdgeOverflow" : false});
        }
        {
            var Q0;
            Q0=makeQuery(id+"F1.opExtrude","CAP_EDGE",EDGE,{"disambiguationData":[OSD([sQuery(id+"F0.wireOp",EDGE,"E1.bottom")])],"isStart":false});
            fillet(context, id + "F15", {"entities" : qUnion([Q0]), "radius" : 2 * mm, "tangentPropagation" : true, "allowEdgeOverflow" : false});
        }
        {
            var Q0;
            {var subQ0=sQuery(id+"F0.wireOp",EDGE,"E21.filletArc");var subQ1=sQuery(id+"F0.wireOp",EDGE,"E7");var subQ2=sQuery(id+"F0.wireOp",EDGE,"E6");var subQ3=sQuery(id+"F0.wireOp",EDGE,"E5");var subQ4=sQuery(id+"F0.wireOp",EDGE,"E4");var subQ5=sQuery(id+"F0.wireOp",EDGE,"E22.filletArc");var subQ6=sQuery(id+"F0.wireOp",EDGE,"E1.bottom");var subQ7=sQuery(id+"F0.wireOp",EDGE,"E1.right");var subQ8=sQuery(id+"F0.wireOp",EDGE,"E1.top");var subQ9=sQuery(id+"F0.wireOp",EDGE,"E1.left");var subQ10=sQuery(id+"F0.wireOp",EDGE,"E23.filletArc");var subQ11=sQuery(id+"F0.wireOp",EDGE,"E24.filletArc");Q0=makeQuery(id+"F2.boolean.opBoolean","SPLIT",FACE,{"disambiguationData":[TD([makeQuery(id+"F1.opExtrude","SWEPT_FACE",FACE,{"disambiguationData":[OSD([subQ6])]})])],"derivedFrom":makeQuery(id+"F1.opExtrude","CAP_FACE",FACE,{"disambiguationData":[OSD([subQ6,subQ8,subQ9,subQ7,subQ4,subQ3,subQ2,subQ1,subQ0,subQ5,subQ10,subQ11])],"isStart":true})});}
            var sketch = newSketch(context, id + "F16", { "sketchPlane" : qUnion([Q0])});
            skLineSegment(sketch, "E79.0", {"start": v(-70, 90) * mm, "end": v(70, 90) * mm});
            skArc(sketch, "E79.1", {"start": v(80, 80) * mm, "mid": v(77.07, 87.07) * mm, "end": v(70, 90) * mm});
            skLineSegment(sketch, "E79.2", {"start": v(80, -80) * mm, "end": v(80, 80) * mm});
            skArc(sketch, "E79.3", {"start": v(70, -90) * mm, "mid": v(77.07, -87.07) * mm, "end": v(80, -80) * mm});
            skLineSegment(sketch, "E79.4", {"start": v(-70, -90) * mm, "end": v(70, -90) * mm});
            skCircle(sketch, "E79.5", {"center": v(60, -67.5) * mm, "radius": 4 * mm});
            skArc(sketch, "E79.6", {"start": v(-56.15, -48.18) * mm, "mid": v(0, -67.5) * mm, "end": v(56.15, -48.18) * mm});
            skArc(sketch, "E79.7", {"start": v(56.15, -48.18) * mm, "mid": v(58.99, -44.68) * mm, "end": v(60, -40.3) * mm});
            skLineSegment(sketch, "E79.8", {"start": v(60, 40.3) * mm, "end": v(60, -40.3) * mm});
            skArc(sketch, "E79.9", {"start": v(-60, -40.3) * mm, "mid": v(-58.99, -44.68) * mm, "end": v(-56.15, -48.18) * mm});
            skLineSegment(sketch, "E79.10", {"start": v(-60, 40.3) * mm, "end": v(-60, -40.3) * mm});
            skCircle(sketch, "E79.11", {"center": v(-60, -67.5) * mm, "radius": 4 * mm});
            skLineSegment(sketch, "E79.12", {"start": v(-80, -80) * mm, "end": v(-80, 80) * mm});
            skArc(sketch, "E79.13", {"start": v(-80, -80) * mm, "mid": v(-77.07, -87.07) * mm, "end": v(-70, -90) * mm});
            skArc(sketch, "E79.14", {"start": v(-56.15, 48.18) * mm, "mid": v(-58.99, 44.68) * mm, "end": v(-60, 40.3) * mm});
            skArc(sketch, "E79.15", {"start": v(56.15, 48.18) * mm, "mid": v(0, 67.5) * mm, "end": v(-56.15, 48.18) * mm});
            skArc(sketch, "E79.16", {"start": v(60, 40.3) * mm, "mid": v(58.99, 44.68) * mm, "end": v(56.15, 48.18) * mm});
            skCircle(sketch, "E79.17", {"center": v(60, 67.5) * mm, "radius": 4 * mm});
            skCircle(sketch, "E79.18", {"center": v(-60, 67.5) * mm, "radius": 4 * mm});
            skArc(sketch, "E79.19", {"start": v(-70, 90) * mm, "mid": v(-77.07, 87.07) * mm, "end": v(-80, 80) * mm});
            skLineSegment(sketch, "E80", {"start": v(0, 90) * mm, "end": v(0, 119.82) * mm, "construction": true});
            skLineSegment(sketch, "E81", {"start": v(-33, 90) * mm, "end": v(-15, 108) * mm});
            skLineSegment(sketch, "E82", {"start": v(-15, 108) * mm, "end": v(-15, 120) * mm});
            skArc(sketch, "E83", {"start": v(-15, 120) * mm, "mid": v(0.09, 134.82) * mm, "end": v(15, 119.82) * mm});
            skLineSegment(sketch, "E84", {"start": v(15, 119.82) * mm, "end": v(15, 108) * mm});
            skLineSegment(sketch, "E85", {"start": v(15, 108) * mm, "end": v(33, 90) * mm});
            skCircle(sketch, "E86", {"center": v(0, 119.82) * mm, "radius": 6 * mm});
            skLineSegment(sketch, "E87", {"start": v(-80, 0) * mm, "end": v(80, 0) * mm, "construction": true});
            skArc(sketch, "E88.MirrorCS", {"start": v(-15, -120) * mm, "mid": v(0.09, -134.82) * mm, "end": v(15, -119.82) * mm});
            skLineSegment(sketch, "E89.MirrorCS", {"start": v(15, -119.82) * mm, "end": v(15, -108) * mm});
            skLineSegment(sketch, "E90.MirrorCS", {"start": v(15, -108) * mm, "end": v(33, -90) * mm});
            skLineSegment(sketch, "E91.MirrorCS", {"start": v(-33, -90) * mm, "end": v(-15, -108) * mm});
            skLineSegment(sketch, "E92.MirrorCS", {"start": v(-15, -108) * mm, "end": v(-15, -120) * mm});
            skCircle(sketch, "E93.MirrorC", {"center": v(0, -119.82) * mm, "radius": 6 * mm});
            skLineSegment(sketch, "E94.MirrorCS", {"start": v(0, -90) * mm, "end": v(0, -119.82) * mm, "construction": true});
            skSolve(sketch);
        }
        {
            var Q0;
            Q0 = qSketchRegion(id + "F16", true);
            var Q1;
            Q1=makeQuery(id+"F2.opExtrude","CAP_FACE",FACE,{"disambiguationData":[OSD([sQuery(id+"F0.wireOp",EDGE,"E12"),sQuery(id+"F0.wireOp",EDGE,"E13"),sQuery(id+"F0.wireOp",EDGE,"E14"),sQuery(id+"F0.wireOp",EDGE,"E15"),sQuery(id+"F0.wireOp",EDGE,"E17.filletArc"),sQuery(id+"F0.wireOp",EDGE,"E18.filletArc"),sQuery(id+"F0.wireOp",EDGE,"E19.filletArc"),sQuery(id+"F0.wireOp",EDGE,"E20.filletArc"),sQuery(id+"F0.wireOp",EDGE,"E25.0"),sQuery(id+"F0.wireOp",EDGE,"E25.1"),sQuery(id+"F0.wireOp",EDGE,"E25.2"),sQuery(id+"F0.wireOp",EDGE,"E25.3"),sQuery(id+"F0.wireOp",EDGE,"E25.4"),sQuery(id+"F0.wireOp",EDGE,"E25.5"),sQuery(id+"F0.wireOp",EDGE,"E25.6"),sQuery(id+"F0.wireOp",EDGE,"E25.7")])],"isStart":false});
            extrude(context, id + "F17", {"entities" : qUnion([Q0]), "endBound" : BoundingType.UP_TO_SURFACE, "endBoundEntityFace" : qUnion([Q1]), "depth" : 25 * mm});
        }
    });
